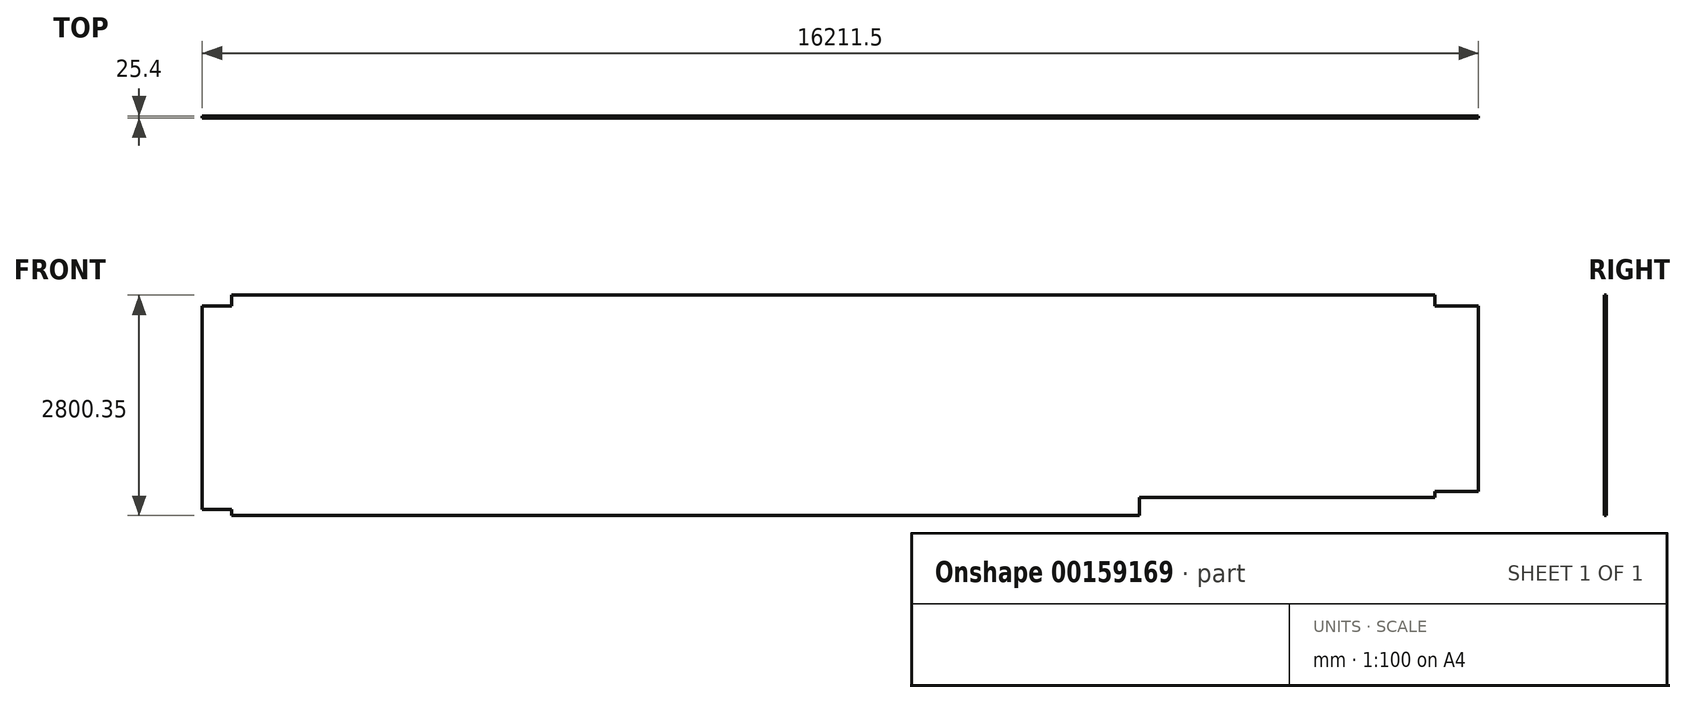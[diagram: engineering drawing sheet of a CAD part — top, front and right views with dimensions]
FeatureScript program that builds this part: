
annotation { "Feature Type Name" : "Feature", "Feature Type Description" : "" }
export const myFeature = defineFeature(function(context is Context, id is Id, definition is map)
    precondition{}
    {
        {
            var Q0;
            Q0=qCreatedBy(makeId("Front.planeOp"),FACE);
            var sketch = newSketch(context, id + "F0", { "sketchPlane" : qUnion([Q0])});
            skLineSegment(sketch, "E0.bottom", {"start": v(374.65, 0) * mm, "end": v(11906.25, 0) * mm});
            skLineSegment(sketch, "E0.top", {"start": v(374.65, 2800.35) * mm, "end": v(15659.1, 2800.35) * mm});
            skLineSegment(sketch, "E0.left", {"start": v(0, 76.2) * mm, "end": v(0, 2660.65) * mm});
            skLineSegment(sketch, "E0.right", {"start": v(16211.55, 304.8) * mm, "end": v(16211.55, 2660.65) * mm});
            skLineSegment(sketch, "E1", {"start": v(16211.55, 304.8) * mm, "end": v(15659.1, 304.8) * mm});
            skLineSegment(sketch, "E2", {"start": v(15659.1, 304.8) * mm, "end": v(15659.1, 228.6) * mm});
            skLineSegment(sketch, "E3", {"start": v(15659.1, 228.6) * mm, "end": v(11906.25, 228.6) * mm});
            skLineSegment(sketch, "E4", {"start": v(11906.25, 228.6) * mm, "end": v(11906.25, 0) * mm});
            skLineSegment(sketch, "E5", {"start": v(16211.55, 2660.65) * mm, "end": v(15659.1, 2660.65) * mm});
            skLineSegment(sketch, "E6", {"start": v(15659.1, 2660.65) * mm, "end": v(15659.1, 2800.35) * mm});
            skLineSegment(sketch, "E7", {"start": v(0, 2660.65) * mm, "end": v(374.65, 2660.65) * mm});
            skLineSegment(sketch, "E8", {"start": v(374.65, 2660.65) * mm, "end": v(374.65, 2800.35) * mm});
            skLineSegment(sketch, "E9", {"start": v(0, 76.2) * mm, "end": v(374.65, 76.2) * mm});
            skLineSegment(sketch, "E10", {"start": v(374.65, 76.2) * mm, "end": v(374.65, 0) * mm});
            skSolve(sketch);
        }
        {
            var Q0;
            Q0 = qSketchRegion(id + "F0", true);
            extrude(context, id + "F1", {"entities" : qUnion([Q0]), "depth" : 25.4 * mm});
        }
    });
